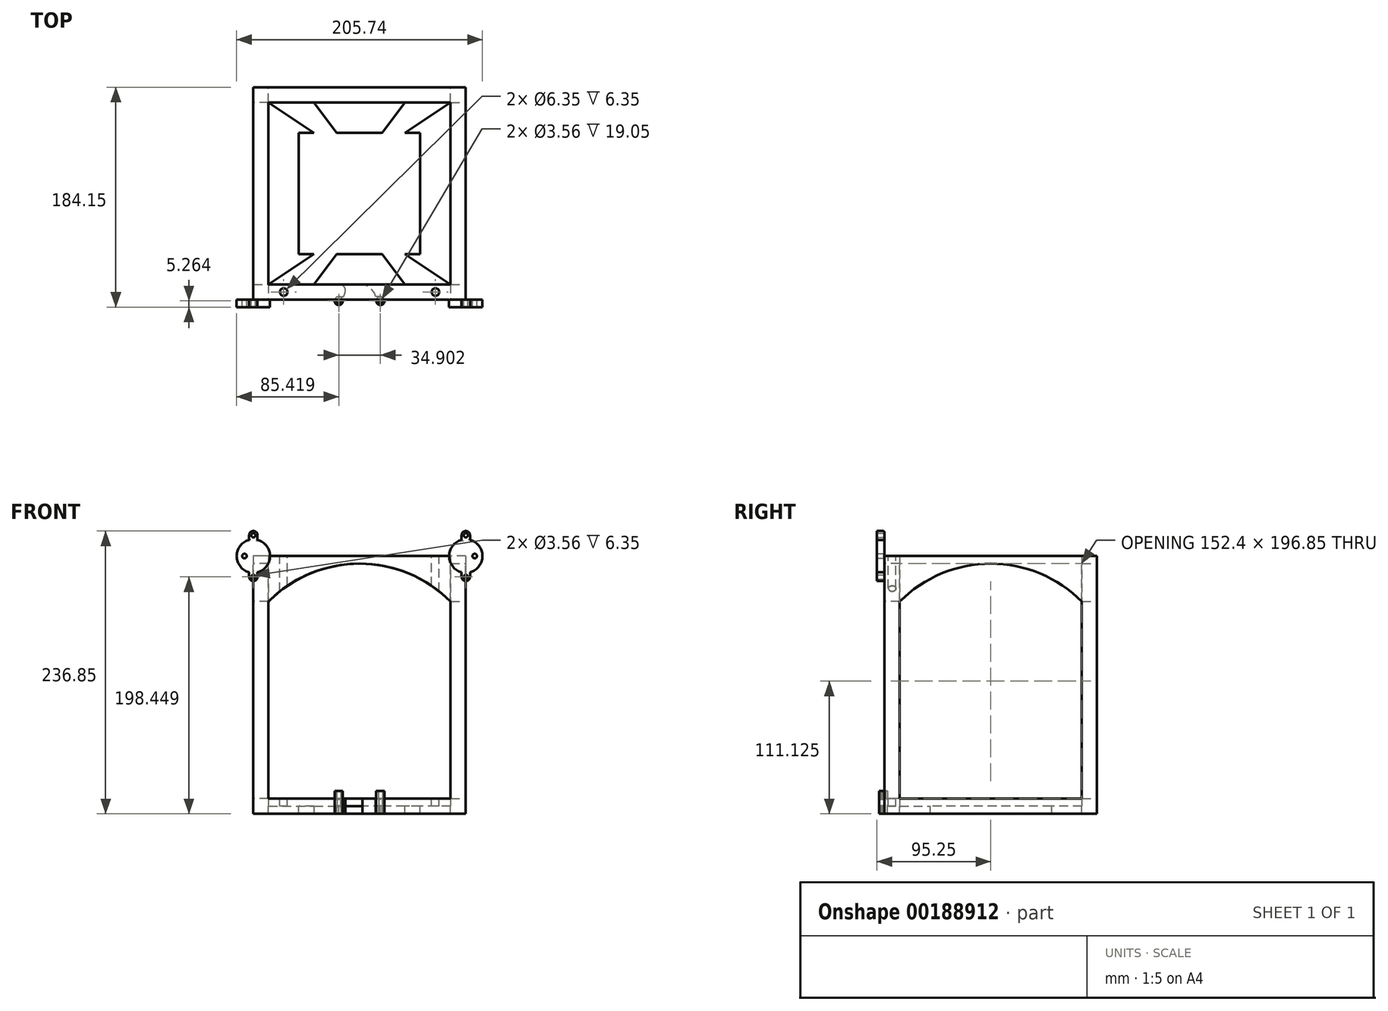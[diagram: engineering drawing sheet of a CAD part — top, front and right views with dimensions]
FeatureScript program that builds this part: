
annotation { "Feature Type Name" : "Feature", "Feature Type Description" : "" }
export const myFeature = defineFeature(function(context is Context, id is Id, definition is map)
    precondition{}
    {
        {
            var Q0;
            Q0=qCreatedBy(makeId("Top.planeOp"),FACE);
            var sketch = newSketch(context, id + "F0", { "sketchPlane" : qUnion([Q0])});
            skLineSegment(sketch, "E0.bottom", {"start": v(50.8, 50.8) * mm, "end": v(-50.8, 50.8) * mm});
            skLineSegment(sketch, "E0.top", {"start": v(50.8, -50.8) * mm, "end": v(-50.8, -50.8) * mm});
            skLineSegment(sketch, "E0.left", {"start": v(50.8, 50.8) * mm, "end": v(50.8, -50.8) * mm});
            skLineSegment(sketch, "E0.right", {"start": v(-50.8, 50.8) * mm, "end": v(-50.8, -50.8) * mm});
            skPoint(sketch, "E0.middle", {"position": v(0, 0) * mm});
            skSolve(sketch);
        }
        {
            var Q0;
            Q0=qSketchRegion(id+"F0",true);
            extrude(context, id + "F1", {"entities" : qUnion([Q0]), "oppositeDirection" : true, "depth" : 6.35 * mm});
        }
        {
            var Q0;
            Q0=qCreatedBy(makeId("Right.planeOp"),FACE);
            var sketch = newSketch(context, id + "F2", { "sketchPlane" : qUnion([Q0])});
            skLineSegment(sketch, "E1.bottom", {"start": v(-76.2, 6.35) * mm, "end": v(-88.9, 6.35) * mm});
            skLineSegment(sketch, "E1.top", {"start": v(-76.2, -6.35) * mm, "end": v(-88.9, -6.35) * mm});
            skLineSegment(sketch, "E1.left", {"start": v(-76.2, 6.35) * mm, "end": v(-76.2, -6.35) * mm});
            skLineSegment(sketch, "E1.right", {"start": v(-88.9, 6.35) * mm, "end": v(-88.9, -6.35) * mm});
            skPoint(sketch, "E1.middle", {"position": v(-82.55, 0) * mm});
            skSolve(sketch);
        }
        {
            var Q0;
            Q0=qSketchRegion(id+"F2",true);
            extrude(context, id + "F3", {"entities" : qUnion([Q0]), "endBound" : BoundingType.SYMMETRIC, "depth" : 177.8 * mm});
        }
        {
            var Q0;
            Q0=makeQuery(id+"F3.opExtrude","SWEPT_BODY",BODY,{"disambiguationData":[OSD([sQuery(id+"F2.wireOp",EDGE,"E1.bottom"),sQuery(id+"F2.wireOp",EDGE,"E1.top"),sQuery(id+"F2.wireOp",EDGE,"E1.left"),sQuery(id+"F2.wireOp",EDGE,"E1.right")])]});
            var Q1;
            Q1=qCreatedBy(makeId("Front.planeOp"),FACE);
            mirror(context, id + "F4", {"entities" : qUnion([Q0]), "mirrorPlane" : qUnion([Q1])});
        }
        {
            var Q0;
            Q0=qCreatedBy(makeId("Front.planeOp"),FACE);
            var sketch = newSketch(context, id + "F5", { "sketchPlane" : qUnion([Q0])});
            skLineSegment(sketch, "E2", {"start": v(76.2, 6.35) * mm, "end": v(76.2, -6.35) * mm});
            skLineSegment(sketch, "E3", {"start": v(76.2, -6.35) * mm, "end": v(88.9, -6.35) * mm});
            skLineSegment(sketch, "E4", {"start": v(88.9, -6.35) * mm, "end": v(88.9, 6.35) * mm});
            skLineSegment(sketch, "E5", {"start": v(88.9, 6.35) * mm, "end": v(76.2, 6.35) * mm});
            skSolve(sketch);
        }
        {
            var Q0;
            Q0=qSketchRegion(id+"F5",true);
            extrude(context, id + "F6", {"entities" : qUnion([Q0]), "endBound" : BoundingType.SYMMETRIC, "depth" : 152.4 * mm});
        }
        {
            var Q0;
            Q0=makeQuery(id+"F6.opExtrude","SWEPT_BODY",BODY,{"disambiguationData":[OSD([sQuery(id+"F5.wireOp",EDGE,"E2"),sQuery(id+"F5.wireOp",EDGE,"E3"),sQuery(id+"F5.wireOp",EDGE,"E4"),sQuery(id+"F5.wireOp",EDGE,"E5")])]});
            var Q1;
            Q1=qCreatedBy(makeId("Right.planeOp"),FACE);
            mirror(context, id + "F7", {"entities" : qUnion([Q0]), "mirrorPlane" : qUnion([Q1])});
        }
        {
            var Q0;
            Q0=makeQuery(id+"F1.opExtrude","SWEPT_FACE",FACE,{"disambiguationData":[OSD([sQuery(id+"F0.wireOp",EDGE,"E0.top")])]});
            var sketch = newSketch(context, id + "F8", { "sketchPlane" : qUnion([Q0])});
            skLineSegment(sketch, "E6", {"start": v(-38.1, 0) * mm, "end": v(-38.1, -6.35) * mm});
            skLineSegment(sketch, "E7", {"start": v(-38.1, -6.35) * mm, "end": v(-19.05, -6.35) * mm});
            skLineSegment(sketch, "E8", {"start": v(-19.05, -6.35) * mm, "end": v(-19.05, 0) * mm});
            skLineSegment(sketch, "E9", {"start": v(-19.05, 0) * mm, "end": v(-38.1, 0) * mm});
            skLineSegment(sketch, "E10.MirrorCS", {"start": v(19.05, -6.35) * mm, "end": v(19.05, 0) * mm, "construction": true});
            skLineSegment(sketch, "E11.MirrorCS", {"start": v(19.05, 0) * mm, "end": v(38.1, 0) * mm, "construction": true});
            skLineSegment(sketch, "E12.MirrorCS", {"start": v(38.1, 0) * mm, "end": v(38.1, -6.35) * mm, "construction": true});
            skLineSegment(sketch, "E13.MirrorCS", {"start": v(38.1, -6.35) * mm, "end": v(19.05, -6.35) * mm, "construction": true});
            skSolve(sketch);
        }
        {
            var Q0;
            Q0=makeQuery(id+"F3.opExtrude","SWEPT_FACE",FACE,{"disambiguationData":[OSD([sQuery(id+"F2.wireOp",EDGE,"E1.left")])]});
            var sketch = newSketch(context, id + "F9", { "sketchPlane" : qUnion([Q0])});
            skLineSegment(sketch, "E14.bottom", {"start": v(-76.2, -6.35) * mm, "end": v(-38.1, -6.35) * mm, "construction": true});
            skLineSegment(sketch, "E14.top", {"start": v(-76.2, 0) * mm, "end": v(-38.1, 0) * mm, "construction": true});
            skLineSegment(sketch, "E14.left", {"start": v(-76.2, -6.35) * mm, "end": v(-76.2, 0) * mm, "construction": true});
            skLineSegment(sketch, "E14.right", {"start": v(-38.1, -6.35) * mm, "end": v(-38.1, 0) * mm, "construction": true});
            skLineSegment(sketch, "E15.MirrorCS", {"start": v(76.2, 0) * mm, "end": v(38.1, 0) * mm});
            skLineSegment(sketch, "E16.MirrorCS", {"start": v(38.1, -6.35) * mm, "end": v(38.1, 0) * mm});
            skLineSegment(sketch, "E17.MirrorCS", {"start": v(76.2, -6.35) * mm, "end": v(38.1, -6.35) * mm});
            skLineSegment(sketch, "E18.MirrorCS", {"start": v(76.2, -6.35) * mm, "end": v(76.2, 0) * mm});
            skSolve(sketch);
        }
        {
            var Q0;
            Q0=makeQuery(id+"F9.imprint","IMPRINT",FACE,{"disambiguationData":[TD([[makeQuery(id+"F9.imprint","IMPRINT",EDGE,{"derivedFrom":sQuery(id+"F9.wireOp",EDGE,"E15.MirrorCS")}),1.0]])]});
            var Q1;
            Q1=makeQuery(id+"F8.imprint","IMPRINT",FACE,{"disambiguationData":[TD([[makeQuery(id+"F8.imprint","IMPRINT",EDGE,{"derivedFrom":sQuery(id+"F8.wireOp",EDGE,"E6")}),1.0]])]});
            loft(context, id + "F10", {"sheetProfilesArray" : [{ "sheetProfileEntities" : qUnion([Q0]) }, { "sheetProfileEntities" : qUnion([Q1]) }]});
        }
        {
            var Q0;
            Q0=makeQuery(id+"F10.opLoft","SWEPT_BODY",BODY,{"disambiguationData":[OSD([makeQuery(id+"F8.imprint","IMPRINT",FACE,{"disambiguationData":[TD([[makeQuery(id+"F8.imprint","IMPRINT",EDGE,{"derivedFrom":sQuery(id+"F8.wireOp",EDGE,"E6")}),1.0]])]}),makeQuery(id+"F9.imprint","IMPRINT",FACE,{"disambiguationData":[TD([[makeQuery(id+"F9.imprint","IMPRINT",EDGE,{"derivedFrom":sQuery(id+"F9.wireOp",EDGE,"E15.MirrorCS")}),1.0]])]})])]});
            var Q1;
            Q1=qCreatedBy(makeId("Right.planeOp"),FACE);
            mirror(context, id + "F11", {"entities" : qUnion([Q0]), "mirrorPlane" : qUnion([Q1])});
        }
        {
            var Q0;
            Q0=makeQuery(id+"F11.opPattern","COPY",BODY,{"derivedFrom":makeQuery(id+"F10.opLoft","SWEPT_BODY",BODY,{"disambiguationData":[OSD([makeQuery(id+"F8.imprint","IMPRINT",FACE,{"disambiguationData":[TD([[makeQuery(id+"F8.imprint","IMPRINT",EDGE,{"derivedFrom":sQuery(id+"F8.wireOp",EDGE,"E6")}),1.0]])]}),makeQuery(id+"F9.imprint","IMPRINT",FACE,{"disambiguationData":[TD([[makeQuery(id+"F9.imprint","IMPRINT",EDGE,{"derivedFrom":sQuery(id+"F9.wireOp",EDGE,"E15.MirrorCS")}),1.0]])]})])]}),"instanceName":"1"});
            var Q1;
            Q1=makeQuery(id+"F10.opLoft","SWEPT_BODY",BODY,{"disambiguationData":[OSD([makeQuery(id+"F8.imprint","IMPRINT",FACE,{"disambiguationData":[TD([[makeQuery(id+"F8.imprint","IMPRINT",EDGE,{"derivedFrom":sQuery(id+"F8.wireOp",EDGE,"E6")}),1.0]])]}),makeQuery(id+"F9.imprint","IMPRINT",FACE,{"disambiguationData":[TD([[makeQuery(id+"F9.imprint","IMPRINT",EDGE,{"derivedFrom":sQuery(id+"F9.wireOp",EDGE,"E15.MirrorCS")}),1.0]])]})])]});
            var Q2;
            Q2=qCreatedBy(makeId("Front.planeOp"),FACE);
            mirror(context, id + "F12", {"entities" : qUnion([Q0, Q1]), "mirrorPlane" : qUnion([Q2])});
        }
        {
            var Q0;
            Q0=makeQuery(id+"F1.opExtrude","SWEPT_BODY",BODY,{"disambiguationData":[OSD([sQuery(id+"F0.wireOp",EDGE,"E0.bottom"),sQuery(id+"F0.wireOp",EDGE,"E0.top"),sQuery(id+"F0.wireOp",EDGE,"E0.left"),sQuery(id+"F0.wireOp",EDGE,"E0.right")])]});
            var Q1;
            Q1=makeQuery(id+"F7.opPattern","COPY",BODY,{"derivedFrom":makeQuery(id+"F6.opExtrude","SWEPT_BODY",BODY,{"disambiguationData":[OSD([sQuery(id+"F5.wireOp",EDGE,"E2"),sQuery(id+"F5.wireOp",EDGE,"E3"),sQuery(id+"F5.wireOp",EDGE,"E4"),sQuery(id+"F5.wireOp",EDGE,"E5")])]}),"instanceName":"1"});
            var Q2;
            Q2=makeQuery(id+"F12.opPattern","COPY",BODY,{"derivedFrom":makeQuery(id+"F10.opLoft","SWEPT_BODY",BODY,{"disambiguationData":[OSD([makeQuery(id+"F8.imprint","IMPRINT",FACE,{"disambiguationData":[TD([[makeQuery(id+"F8.imprint","IMPRINT",EDGE,{"derivedFrom":sQuery(id+"F8.wireOp",EDGE,"E6")}),1.0]])]}),makeQuery(id+"F9.imprint","IMPRINT",FACE,{"disambiguationData":[TD([[makeQuery(id+"F9.imprint","IMPRINT",EDGE,{"derivedFrom":sQuery(id+"F9.wireOp",EDGE,"E15.MirrorCS")}),1.0]])]})])]}),"instanceName":"1"});
            var Q3;
            Q3=makeQuery(id+"F4.opPattern","COPY",BODY,{"derivedFrom":makeQuery(id+"F3.opExtrude","SWEPT_BODY",BODY,{"disambiguationData":[OSD([sQuery(id+"F2.wireOp",EDGE,"E1.bottom"),sQuery(id+"F2.wireOp",EDGE,"E1.top"),sQuery(id+"F2.wireOp",EDGE,"E1.left"),sQuery(id+"F2.wireOp",EDGE,"E1.right")])]}),"instanceName":"1"});
            var Q4;
            Q4=makeQuery(id+"F3.opExtrude","SWEPT_BODY",BODY,{"disambiguationData":[OSD([sQuery(id+"F2.wireOp",EDGE,"E1.bottom"),sQuery(id+"F2.wireOp",EDGE,"E1.top"),sQuery(id+"F2.wireOp",EDGE,"E1.left"),sQuery(id+"F2.wireOp",EDGE,"E1.right")])]});
            var Q5;
            Q5=makeQuery(id+"F6.opExtrude","SWEPT_BODY",BODY,{"disambiguationData":[OSD([sQuery(id+"F5.wireOp",EDGE,"E2"),sQuery(id+"F5.wireOp",EDGE,"E3"),sQuery(id+"F5.wireOp",EDGE,"E4"),sQuery(id+"F5.wireOp",EDGE,"E5")])]});
            var Q6;
            Q6=makeQuery(id+"F11.opPattern","COPY",BODY,{"derivedFrom":makeQuery(id+"F10.opLoft","SWEPT_BODY",BODY,{"disambiguationData":[OSD([makeQuery(id+"F8.imprint","IMPRINT",FACE,{"disambiguationData":[TD([[makeQuery(id+"F8.imprint","IMPRINT",EDGE,{"derivedFrom":sQuery(id+"F8.wireOp",EDGE,"E6")}),1.0]])]}),makeQuery(id+"F9.imprint","IMPRINT",FACE,{"disambiguationData":[TD([[makeQuery(id+"F9.imprint","IMPRINT",EDGE,{"derivedFrom":sQuery(id+"F9.wireOp",EDGE,"E15.MirrorCS")}),1.0]])]})])]}),"instanceName":"1"});
            var Q7;
            Q7=makeQuery(id+"F10.opLoft","SWEPT_BODY",BODY,{"disambiguationData":[OSD([makeQuery(id+"F8.imprint","IMPRINT",FACE,{"disambiguationData":[TD([[makeQuery(id+"F8.imprint","IMPRINT",EDGE,{"derivedFrom":sQuery(id+"F8.wireOp",EDGE,"E6")}),1.0]])]}),makeQuery(id+"F9.imprint","IMPRINT",FACE,{"disambiguationData":[TD([[makeQuery(id+"F9.imprint","IMPRINT",EDGE,{"derivedFrom":sQuery(id+"F9.wireOp",EDGE,"E15.MirrorCS")}),1.0]])]})])]});
            var Q8;
            Q8=makeQuery(id+"F12.opPattern","COPY",BODY,{"derivedFrom":makeQuery(id+"F11.opPattern","COPY",BODY,{"derivedFrom":makeQuery(id+"F10.opLoft","SWEPT_BODY",BODY,{"disambiguationData":[OSD([makeQuery(id+"F8.imprint","IMPRINT",FACE,{"disambiguationData":[TD([[makeQuery(id+"F8.imprint","IMPRINT",EDGE,{"derivedFrom":sQuery(id+"F8.wireOp",EDGE,"E6")}),1.0]])]}),makeQuery(id+"F9.imprint","IMPRINT",FACE,{"disambiguationData":[TD([[makeQuery(id+"F9.imprint","IMPRINT",EDGE,{"derivedFrom":sQuery(id+"F9.wireOp",EDGE,"E15.MirrorCS")}),1.0]])]})])]}),"instanceName":"1"}),"instanceName":"1"});
            booleanBodies(context, id + "F13", {"operationType" : BooleanOperationType.UNION, "tools" : qUnion([Q0, Q1, Q2, Q3, Q4, Q5, Q6, Q7, Q8])});
        }
        {
            var Q0;
            {var subQ0=makeQuery(id+"F6.opExtrude","SWEPT_FACE",FACE,{"disambiguationData":[OSD([sQuery(id+"F5.wireOp",EDGE,"E5")])]});var subQ1=makeQuery(id+"F3.opExtrude","SWEPT_FACE",FACE,{"disambiguationData":[OSD([sQuery(id+"F2.wireOp",EDGE,"E1.bottom")])]});Q0=makeQuery(id+"F13.opBoolean","MERGE",FACE,{"derivedFrom":[subQ1,makeQuery(id+"F4.opPattern","COPY",FACE,{"derivedFrom":subQ1,"instanceName":"1"}),subQ0,makeQuery(id+"F7.opPattern","COPY",FACE,{"derivedFrom":subQ0,"instanceName":"1"})]});}
            var sketch = newSketch(context, id + "F14", { "sketchPlane" : qUnion([Q0])});
            skLineSegment(sketch, "E19.bottom", {"start": v(-76.2, 76.2) * mm, "end": v(-88.9, 76.2) * mm});
            skLineSegment(sketch, "E19.top", {"start": v(-76.2, 88.9) * mm, "end": v(-88.9, 88.9) * mm});
            skLineSegment(sketch, "E19.left", {"start": v(-76.2, 76.2) * mm, "end": v(-76.2, 88.9) * mm});
            skLineSegment(sketch, "E19.right", {"start": v(-88.9, 76.2) * mm, "end": v(-88.9, 88.9) * mm});
            skLineSegment(sketch, "E20.bottom", {"start": v(76.2, 76.2) * mm, "end": v(88.9, 76.2) * mm});
            skLineSegment(sketch, "E20.top", {"start": v(76.2, 88.9) * mm, "end": v(88.9, 88.9) * mm});
            skLineSegment(sketch, "E20.left", {"start": v(76.2, 76.2) * mm, "end": v(76.2, 88.9) * mm});
            skLineSegment(sketch, "E20.right", {"start": v(88.9, 76.2) * mm, "end": v(88.9, 88.9) * mm});
            skLineSegment(sketch, "E21.bottom", {"start": v(76.2, -76.2) * mm, "end": v(88.9, -76.2) * mm});
            skLineSegment(sketch, "E21.top", {"start": v(76.2, -88.9) * mm, "end": v(88.9, -88.9) * mm});
            skLineSegment(sketch, "E21.left", {"start": v(76.2, -76.2) * mm, "end": v(76.2, -88.9) * mm});
            skLineSegment(sketch, "E21.right", {"start": v(88.9, -76.2) * mm, "end": v(88.9, -88.9) * mm});
            skLineSegment(sketch, "E22.bottom", {"start": v(-88.9, -88.9) * mm, "end": v(-76.2, -88.9) * mm});
            skLineSegment(sketch, "E22.top", {"start": v(-88.9, -76.2) * mm, "end": v(-76.2, -76.2) * mm});
            skLineSegment(sketch, "E22.left", {"start": v(-88.9, -88.9) * mm, "end": v(-88.9, -76.2) * mm});
            skLineSegment(sketch, "E22.right", {"start": v(-76.2, -88.9) * mm, "end": v(-76.2, -76.2) * mm});
            skSolve(sketch);
        }
        {
            var Q0;
            Q0=qSketchRegion(id+"F14",true);
            extrude(context, id + "F15", {"entities" : qUnion([Q0]), "operationType" : NewBodyOperationType.ADD, "depth" : 203.2 * mm});
        }
        {
            var Q0;
            {var subQ0=makeQuery(id+"F3.opExtrude","CAP_FACE",FACE,{"disambiguationData":[OSD([sQuery(id+"F2.wireOp",EDGE,"E1.bottom"),sQuery(id+"F2.wireOp",EDGE,"E1.top"),sQuery(id+"F2.wireOp",EDGE,"E1.left"),sQuery(id+"F2.wireOp",EDGE,"E1.right")])],"isStart":true});Q0=makeQuery(id+"F15.boolean.opBoolean","MERGE",FACE,{"derivedFrom":[makeQuery(id+"F13.opBoolean","MERGE",FACE,{"derivedFrom":[subQ0,makeQuery(id+"F4.opPattern","COPY",FACE,{"derivedFrom":subQ0,"instanceName":"1"}),makeQuery(id+"F7.opPattern","COPY",FACE,{"derivedFrom":makeQuery(id+"F6.opExtrude","SWEPT_FACE",FACE,{"disambiguationData":[OSD([sQuery(id+"F5.wireOp",EDGE,"E4")])]}),"instanceName":"1"})]}),makeQuery(id+"F15.opExtrude","SWEPT_FACE",FACE,{"disambiguationData":[OSD([sQuery(id+"F14.wireOp",EDGE,"E19.right")])]}),makeQuery(id+"F15.opExtrude","SWEPT_FACE",FACE,{"disambiguationData":[OSD([sQuery(id+"F14.wireOp",EDGE,"E22.left")])]})]});}
            var sketch = newSketch(context, id + "F16", { "sketchPlane" : qUnion([Q0])});
            skArc(sketch, "E23", {"start": v(76.2, 171.45) * mm, "mid": v(0, 203.2) * mm, "end": v(-76.2, 171.45) * mm});
            skLineSegment(sketch, "E24", {"start": v(-76.2, 209.55) * mm, "end": v(76.2, 209.55) * mm});
            skLineSegment(sketch, "E25", {"start": v(76.2, 209.55) * mm, "end": v(76.2, 171.45) * mm});
            skLineSegment(sketch, "E26", {"start": v(-76.2, 209.55) * mm, "end": v(-76.2, 171.45) * mm});
            skSolve(sketch);
        }
        {
            var Q0;
            Q0=qSketchRegion(id+"F16",true);
            extrude(context, id + "F17", {"entities" : qUnion([Q0]), "oppositeDirection" : true, "depth" : 12.7 * mm});
        }
        {
            var Q0;
            Q0=makeQuery(id+"F17.opExtrude","SWEPT_BODY",BODY,{"disambiguationData":[OSD([sQuery(id+"F16.wireOp",EDGE,"E23"),sQuery(id+"F16.wireOp",EDGE,"E24"),sQuery(id+"F16.wireOp",EDGE,"E25"),sQuery(id+"F16.wireOp",EDGE,"E26")])]});
            var Q1;
            Q1=qCreatedBy(makeId("Right.planeOp"),FACE);
            mirror(context, id + "F18", {"operationType" : NewBodyOperationType.ADD, "entities" : qUnion([Q0]), "mirrorPlane" : qUnion([Q1])});
        }
        {
            var Q0;
            Q0=makeQuery(id+"F15.boolean.opBoolean","MERGE",FACE,{"derivedFrom":[makeQuery(id+"F4.opPattern","COPY",FACE,{"derivedFrom":makeQuery(id+"F3.opExtrude","SWEPT_FACE",FACE,{"disambiguationData":[OSD([sQuery(id+"F2.wireOp",EDGE,"E1.right")])]}),"instanceName":"1"}),makeQuery(id+"F15.opExtrude","SWEPT_FACE",FACE,{"disambiguationData":[OSD([sQuery(id+"F14.wireOp",EDGE,"E19.top")])]}),makeQuery(id+"F15.opExtrude","SWEPT_FACE",FACE,{"disambiguationData":[OSD([sQuery(id+"F14.wireOp",EDGE,"E20.top")])]})]});
            var sketch = newSketch(context, id + "F19", { "sketchPlane" : qUnion([Q0])});
            skArc(sketch, "E27", {"start": v(76.2, 171.45) * mm, "mid": v(0, 203.2) * mm, "end": v(-76.2, 171.45) * mm});
            skLineSegment(sketch, "E28", {"start": v(-76.2, 171.45) * mm, "end": v(-76.2, 209.55) * mm});
            skLineSegment(sketch, "E29", {"start": v(-76.2, 209.55) * mm, "end": v(76.2, 209.55) * mm});
            skLineSegment(sketch, "E30", {"start": v(76.2, 209.55) * mm, "end": v(76.2, 171.45) * mm});
            skSolve(sketch);
        }
        {
            var Q0;
            Q0=qSketchRegion(id+"F19",true);
            extrude(context, id + "F20", {"entities" : qUnion([Q0]), "oppositeDirection" : true, "depth" : 12.7 * mm});
        }
        {
            var Q0;
            Q0=makeQuery(id+"F20.opExtrude","SWEPT_BODY",BODY,{"disambiguationData":[OSD([sQuery(id+"F19.wireOp",EDGE,"E27"),sQuery(id+"F19.wireOp",EDGE,"E28"),sQuery(id+"F19.wireOp",EDGE,"E29"),sQuery(id+"F19.wireOp",EDGE,"E30")])]});
            var Q1;
            Q1=qCreatedBy(makeId("Front.planeOp"),FACE);
            mirror(context, id + "F21", {"operationType" : NewBodyOperationType.ADD, "entities" : qUnion([Q0]), "mirrorPlane" : qUnion([Q1])});
        }
        {
            var Q0;
            {var subQ0=makeQuery(id+"F20.opExtrude","SWEPT_FACE",FACE,{"disambiguationData":[OSD([sQuery(id+"F19.wireOp",EDGE,"E29")])]});var subQ1=makeQuery(id+"F17.opExtrude","SWEPT_FACE",FACE,{"disambiguationData":[OSD([sQuery(id+"F16.wireOp",EDGE,"E24")])]});Q0=makeQuery(id+"F21.boolean.opBoolean","MERGE",FACE,{"derivedFrom":[makeQuery(id+"F18.boolean.opBoolean","MERGE",FACE,{"derivedFrom":[makeQuery(id+"F15.opExtrude","CAP_FACE",FACE,{"disambiguationData":[OSD([sQuery(id+"F14.wireOp",EDGE,"E19.bottom"),sQuery(id+"F14.wireOp",EDGE,"E19.top"),sQuery(id+"F14.wireOp",EDGE,"E19.left"),sQuery(id+"F14.wireOp",EDGE,"E19.right")])],"isStart":false}),makeQuery(id+"F15.opExtrude","CAP_FACE",FACE,{"disambiguationData":[OSD([sQuery(id+"F14.wireOp",EDGE,"E22.bottom"),sQuery(id+"F14.wireOp",EDGE,"E22.top"),sQuery(id+"F14.wireOp",EDGE,"E22.left"),sQuery(id+"F14.wireOp",EDGE,"E22.right")])],"isStart":false}),subQ1]}),makeQuery(id+"F18.boolean.opBoolean","MERGE",FACE,{"derivedFrom":[makeQuery(id+"F15.opExtrude","CAP_FACE",FACE,{"disambiguationData":[OSD([sQuery(id+"F14.wireOp",EDGE,"E20.bottom"),sQuery(id+"F14.wireOp",EDGE,"E20.top"),sQuery(id+"F14.wireOp",EDGE,"E20.left"),sQuery(id+"F14.wireOp",EDGE,"E20.right")])],"isStart":false}),makeQuery(id+"F15.opExtrude","CAP_FACE",FACE,{"disambiguationData":[OSD([sQuery(id+"F14.wireOp",EDGE,"E21.bottom"),sQuery(id+"F14.wireOp",EDGE,"E21.top"),sQuery(id+"F14.wireOp",EDGE,"E21.left"),sQuery(id+"F14.wireOp",EDGE,"E21.right")])],"isStart":false}),makeQuery(id+"F18.opPattern","COPY",FACE,{"derivedFrom":subQ1,"instanceName":"1"})]}),subQ0,makeQuery(id+"F21.opPattern","COPY",FACE,{"derivedFrom":subQ0,"instanceName":"1"})]});}
            var sketch = newSketch(context, id + "F22", { "sketchPlane" : qUnion([Q0])});
            skCircle(sketch, "E31", {"center": v(-63.5, -82.55) * mm, "radius": 3.18 * mm});
            skCircle(sketch, "E32", {"center": v(63.5, -82.55) * mm, "radius": 3.18 * mm});
            skLineSegment(sketch, "E33", {"start": v(-63.5, -82.55) * mm, "end": v(63.5, -82.55) * mm, "construction": true});
            skLineSegment(sketch, "E34", {"start": v(63.5, -82.55) * mm, "end": v(0, 0) * mm, "construction": true});
            skLineSegment(sketch, "E35", {"start": v(0, 0) * mm, "end": v(-63.5, -82.55) * mm, "construction": true});
            skLineSegment(sketch, "E36", {"start": v(0, -76.2) * mm, "end": v(0, -82.55) * mm, "construction": true});
            skLineSegment(sketch, "E37", {"start": v(0, -82.55) * mm, "end": v(0, -88.9) * mm, "construction": true});
            skSolve(sketch);
        }
        {
            var Q0;
            Q0=qSketchRegion(id+"F22",true);
            extrude(context, id + "F23", {"entities" : qUnion([Q0]), "operationType" : NewBodyOperationType.REMOVE, "oppositeDirection" : true, "depth" : 209.55 * mm});
        }
        {
            var Q0;
            {var subQ0=sQuery(id+"F2.wireOp",EDGE,"E1.top");var subQ1=sQuery(id+"F0.wireOp",EDGE,"E0.top");var subQ2=makeQuery(id+"F10.opLoft","SWEPT_FACE",FACE,{"disambiguationData":[OSD([subQ1,subQ0,sQuery(id+"F2.wireOp",EDGE,"E1.left"),sQuery(id+"F8.wireOp",EDGE,"E6"),sQuery(id+"F8.wireOp",EDGE,"E7"),sQuery(id+"F8.wireOp",EDGE,"E8"),sQuery(id+"F9.wireOp",EDGE,"E16.MirrorCS"),sQuery(id+"F9.wireOp",EDGE,"E17.MirrorCS"),sQuery(id+"F9.wireOp",EDGE,"E18.MirrorCS")])]});var subQ3=makeQuery(id+"F11.opPattern","COPY",FACE,{"derivedFrom":subQ2,"instanceName":"1"});var subQ4=makeQuery(id+"F6.opExtrude","SWEPT_FACE",FACE,{"disambiguationData":[OSD([sQuery(id+"F5.wireOp",EDGE,"E3")])]});var subQ5=makeQuery(id+"F3.opExtrude","SWEPT_FACE",FACE,{"disambiguationData":[OSD([subQ0])]});Q0=makeQuery(id+"F13.opBoolean","MERGE",FACE,{"derivedFrom":[makeQuery(id+"F1.opExtrude","CAP_FACE",FACE,{"disambiguationData":[OSD([sQuery(id+"F0.wireOp",EDGE,"E0.bottom"),subQ1,sQuery(id+"F0.wireOp",EDGE,"E0.left"),sQuery(id+"F0.wireOp",EDGE,"E0.right")])],"isStart":false}),subQ5,makeQuery(id+"F4.opPattern","COPY",FACE,{"derivedFrom":subQ5,"instanceName":"1"}),subQ4,makeQuery(id+"F7.opPattern","COPY",FACE,{"derivedFrom":subQ4,"instanceName":"1"}),subQ2,subQ3,makeQuery(id+"F12.opPattern","COPY",FACE,{"derivedFrom":subQ2,"instanceName":"1"}),makeQuery(id+"F12.opPattern","COPY",FACE,{"derivedFrom":subQ3,"instanceName":"1"})]});}
            var sketch = newSketch(context, id + "F24", { "sketchPlane" : qUnion([Q0])});
            skCircle(sketch, "E38", {"center": v(0, 82.55) * mm, "radius": 1.9 * mm});
            skArc(sketch, "E39", {"start": v(13.52, 93.49) * mm, "mid": v(0, 103.96) * mm, "end": v(-13.52, 93.49) * mm});
            skArc(sketch, "E40", {"start": v(17.45, 86.49) * mm, "mid": v(20.95, 89.99) * mm, "end": v(17.45, 93.49) * mm});
            skArc(sketch, "E41", {"start": v(-17.45, 93.49) * mm, "mid": v(-20.95, 89.99) * mm, "end": v(-17.45, 86.49) * mm});
            skLineSegment(sketch, "E42", {"start": v(17.45, 89.99) * mm, "end": v(0, 89.99) * mm, "construction": true});
            skLineSegment(sketch, "E43", {"start": v(0, 89.99) * mm, "end": v(-17.45, 89.99) * mm, "construction": true});
            skLineSegment(sketch, "E44", {"start": v(0, 82.55) * mm, "end": v(0, 76.02) * mm, "construction": true});
            skLineSegment(sketch, "E45", {"start": v(17.45, 89.99) * mm, "end": v(0, 82.55) * mm, "construction": true});
            skLineSegment(sketch, "E46", {"start": v(0, 82.55) * mm, "end": v(-17.45, 89.99) * mm, "construction": true});
            skLineSegment(sketch, "E47", {"start": v(17.45, 93.49) * mm, "end": v(13.52, 93.49) * mm});
            skLineSegment(sketch, "E48", {"start": v(17.45, 86.49) * mm, "end": v(13.52, 86.49) * mm});
            skLineSegment(sketch, "E49", {"start": v(17.45, 93.49) * mm, "end": v(17.45, 89.99) * mm, "construction": true});
            skLineSegment(sketch, "E50", {"start": v(17.45, 86.49) * mm, "end": v(17.45, 89.99) * mm, "construction": true});
            skLineSegment(sketch, "E51", {"start": v(-17.45, 93.49) * mm, "end": v(-13.52, 93.49) * mm});
            skLineSegment(sketch, "E52", {"start": v(-17.45, 86.49) * mm, "end": v(-13.52, 86.49) * mm});
            skLineSegment(sketch, "E53", {"start": v(-17.45, 93.49) * mm, "end": v(-17.45, 89.99) * mm, "construction": true});
            skLineSegment(sketch, "E54", {"start": v(-17.45, 89.99) * mm, "end": v(-17.45, 86.49) * mm, "construction": true});
            skArc(sketch, "E55.trimOffspring", {"start": v(-13.52, 86.49) * mm, "mid": v(0, 76.02) * mm, "end": v(13.52, 86.49) * mm});
            skCircle(sketch, "E56", {"center": v(17.45, 89.99) * mm, "radius": 1.78 * mm});
            skCircle(sketch, "E57.MirrorC", {"center": v(-17.45, 89.99) * mm, "radius": 1.78 * mm});
            skPoint(sketch, "E58", {"position": v(0, 88.9) * mm});
            skLineSegment(sketch, "E59", {"start": v(0, 88.9) * mm, "end": v(0, 82.55) * mm, "construction": true});
            skLineSegment(sketch, "E60", {"start": v(0, 82.55) * mm, "end": v(0, 76.2) * mm, "construction": true});
            skSolve(sketch);
        }
        {
            var Q0;
            Q0=qSketchRegion(id+"F24",true);
            extrude(context, id + "F25", {"entities" : qUnion([Q0]), "operationType" : NewBodyOperationType.ADD, "oppositeDirection" : true, "depth" : 19.05 * mm});
        }
        {
            var Q0;
            Q0=makeQuery(id+"F25.opExtrude","CAP_FACE",FACE,{"disambiguationData":[OSD([sQuery(id+"F24.wireOp",EDGE,"E38"),sQuery(id+"F24.wireOp",EDGE,"E39"),sQuery(id+"F24.wireOp",EDGE,"E40"),sQuery(id+"F24.wireOp",EDGE,"E41"),sQuery(id+"F24.wireOp",EDGE,"E47"),sQuery(id+"F24.wireOp",EDGE,"E48"),sQuery(id+"F24.wireOp",EDGE,"E51"),sQuery(id+"F24.wireOp",EDGE,"E52"),sQuery(id+"F24.wireOp",EDGE,"E55.trimOffspring"),sQuery(id+"F24.wireOp",EDGE,"E56"),sQuery(id+"F24.wireOp",EDGE,"E57.MirrorC")])],"isStart":false});
            var sketch = newSketch(context, id + "F26", { "sketchPlane" : qUnion([Q0])});
            skArc(sketch, "E61", {"start": v(-13.97, -89.66) * mm, "mid": v(-13.97, -89.99) * mm, "end": v(-13.97, -90.31) * mm});
            skArc(sketch, "E62", {"start": v(-17.45, -93.49) * mm, "mid": v(-15.1, -92.57) * mm, "end": v(-13.97, -90.31) * mm});
            skArc(sketch, "E63", {"start": v(17.45, -86.49) * mm, "mid": v(13.95, -89.99) * mm, "end": v(17.45, -93.49) * mm});
            skLineSegment(sketch, "E64", {"start": v(-17.45, -86.49) * mm, "end": v(-13.52, -86.49) * mm});
            skLineSegment(sketch, "E65", {"start": v(-17.45, -93.49) * mm, "end": v(-13.52, -93.49) * mm});
            skLineSegment(sketch, "E66", {"start": v(17.45, -93.49) * mm, "end": v(13.52, -93.49) * mm});
            skLineSegment(sketch, "E67", {"start": v(13.52, -86.49) * mm, "end": v(17.45, -86.49) * mm});
            skArc(sketch, "E68.trimOffspring", {"start": v(-13.52, -93.49) * mm, "mid": v(0, -103.96) * mm, "end": v(13.52, -93.49) * mm});
            skArc(sketch, "E69.trimOffspring", {"start": v(13.52, -86.49) * mm, "mid": v(0, -76.02) * mm, "end": v(-13.52, -86.49) * mm});
            skArc(sketch, "E70.trimOffspring", {"start": v(-13.97, -89.66) * mm, "mid": v(-15.1, -87.4) * mm, "end": v(-17.45, -86.49) * mm});
            skSolve(sketch);
        }
        {
            var Q0;
            Q0=qSketchRegion(id+"F26",true);
            extrude(context, id + "F27", {"entities" : qUnion([Q0]), "operationType" : NewBodyOperationType.REMOVE, "oppositeDirection" : true, "depth" : 25.4 * mm});
        }
        {
            var Q0;
            Q0=makeQuery(id+"F25.boolean.opBoolean","INTERSECT",EDGE,{"disambiguationData":[OD(1.0)],"derivedFrom":[makeQuery(id+"F3.opExtrude","SWEPT_FACE",FACE,{"disambiguationData":[OSD([sQuery(id+"F2.wireOp",EDGE,"E1.left")])]}),makeQuery(id+"F25.opExtrude","SWEPT_FACE",FACE,{"disambiguationData":[OSD([sQuery(id+"F24.wireOp",EDGE,"E55.trimOffspring")])]})]});
            var Q1;
            Q1=makeQuery(id+"F25.boolean.opBoolean","INTERSECT",EDGE,{"disambiguationData":[OD(0.0)],"derivedFrom":[makeQuery(id+"F3.opExtrude","SWEPT_FACE",FACE,{"disambiguationData":[OSD([sQuery(id+"F2.wireOp",EDGE,"E1.left")])]}),makeQuery(id+"F25.opExtrude","SWEPT_FACE",FACE,{"disambiguationData":[OSD([sQuery(id+"F24.wireOp",EDGE,"E55.trimOffspring")])]})]});
            fillet(context, id + "F28", {"entities" : qUnion([Q0, Q1]), "radius" : 5.08 * mm, "tangentPropagation" : true, "allowEdgeOverflow" : false});
        }
        {
            var Q0;
            {var subQ1=makeQuery(id+"F6.opExtrude","SWEPT_FACE",FACE,{"disambiguationData":[OSD([sQuery(id+"F5.wireOp",EDGE,"E4")])]});var subQ12=sQuery(id+"F2.wireOp",EDGE,"E1.right");var subQ16=sQuery(id+"F14.wireOp",EDGE,"E22.bottom");var subQ19=sQuery(id+"F19.wireOp",EDGE,"E29");var subQ30=sQuery(id+"F19.wireOp",EDGE,"E27");var subQ33=sQuery(id+"F14.wireOp",EDGE,"E21.top");Q0=makeQuery(id+"F25.boolean.opBoolean","SPLIT",FACE,{"disambiguationData":[TD([subQ1])],"derivedFrom":makeQuery(id+"F21.boolean.opBoolean","MERGE",FACE,{"derivedFrom":[makeQuery(id+"F15.boolean.opBoolean","MERGE",FACE,{"derivedFrom":[makeQuery(id+"F3.opExtrude","SWEPT_FACE",FACE,{"disambiguationData":[OSD([subQ12])]}),makeQuery(id+"F15.opExtrude","SWEPT_FACE",FACE,{"disambiguationData":[OSD([subQ33])]}),makeQuery(id+"F15.opExtrude","SWEPT_FACE",FACE,{"disambiguationData":[OSD([subQ16])]})]}),makeQuery(id+"F21.opPattern","COPY",FACE,{"derivedFrom":makeQuery(id+"F20.opExtrude","CAP_FACE",FACE,{"disambiguationData":[OSD([subQ30,sQuery(id+"F19.wireOp",EDGE,"E28"),subQ19,sQuery(id+"F19.wireOp",EDGE,"E30")])],"isStart":true}),"instanceName":"1"})]})});}
            var sketch = newSketch(context, id + "F29", { "sketchPlane" : qUnion([Q0])});
            skCircle(sketch, "E71", {"center": v(-96.34, 209.55) * mm, "radius": 1.9 * mm});
            skArc(sketch, "E72", {"start": v(-85.4, 196.03) * mm, "mid": v(-74.93, 209.55) * mm, "end": v(-85.4, 223.07) * mm});
            skArc(sketch, "E73", {"start": v(-92.4, 192.1) * mm, "mid": v(-88.9, 188.6) * mm, "end": v(-85.4, 192.1) * mm});
            skArc(sketch, "E74", {"start": v(-85.4, 227) * mm, "mid": v(-88.9, 230.5) * mm, "end": v(-92.4, 227) * mm});
            skLineSegment(sketch, "E75", {"start": v(-88.9, 192.1) * mm, "end": v(-88.9, 209.55) * mm, "construction": true});
            skLineSegment(sketch, "E76", {"start": v(-88.9, 209.55) * mm, "end": v(-88.9, 227) * mm, "construction": true});
            skLineSegment(sketch, "E77", {"start": v(-96.34, 209.55) * mm, "end": v(-102.87, 209.55) * mm, "construction": true});
            skLineSegment(sketch, "E78", {"start": v(-88.9, 192.1) * mm, "end": v(-96.34, 209.55) * mm, "construction": true});
            skLineSegment(sketch, "E79", {"start": v(-96.34, 209.55) * mm, "end": v(-88.9, 227) * mm, "construction": true});
            skLineSegment(sketch, "E80", {"start": v(-85.4, 192.1) * mm, "end": v(-85.4, 196.03) * mm});
            skLineSegment(sketch, "E81", {"start": v(-92.4, 192.1) * mm, "end": v(-92.4, 196.03) * mm});
            skLineSegment(sketch, "E82", {"start": v(-85.4, 192.1) * mm, "end": v(-88.9, 192.1) * mm, "construction": true});
            skLineSegment(sketch, "E83", {"start": v(-92.4, 192.1) * mm, "end": v(-88.9, 192.1) * mm, "construction": true});
            skLineSegment(sketch, "E84", {"start": v(-85.4, 227) * mm, "end": v(-85.4, 223.07) * mm});
            skLineSegment(sketch, "E85", {"start": v(-92.4, 227) * mm, "end": v(-92.4, 223.07) * mm});
            skLineSegment(sketch, "E86", {"start": v(-85.4, 227) * mm, "end": v(-88.9, 227) * mm, "construction": true});
            skLineSegment(sketch, "E87", {"start": v(-88.9, 227) * mm, "end": v(-92.4, 227) * mm, "construction": true});
            skArc(sketch, "E88.trimOffspring", {"start": v(-92.4, 223.07) * mm, "mid": v(-102.87, 209.55) * mm, "end": v(-92.4, 196.03) * mm});
            skCircle(sketch, "E89", {"center": v(-88.9, 192.1) * mm, "radius": 1.78 * mm});
            skCircle(sketch, "E90.MirrorC", {"center": v(-88.9, 227) * mm, "radius": 1.78 * mm});
            skCircle(sketch, "E91", {"center": v(96.34, 209.55) * mm, "radius": 1.9 * mm});
            skArc(sketch, "E92", {"start": v(85.4, 223.07) * mm, "mid": v(74.93, 209.55) * mm, "end": v(85.4, 196.03) * mm});
            skArc(sketch, "E93", {"start": v(92.4, 227) * mm, "mid": v(88.9, 230.5) * mm, "end": v(85.4, 227) * mm});
            skArc(sketch, "E94", {"start": v(85.4, 192.1) * mm, "mid": v(88.9, 188.6) * mm, "end": v(92.4, 192.1) * mm});
            skLineSegment(sketch, "E95", {"start": v(88.9, 227) * mm, "end": v(88.9, 209.55) * mm, "construction": true});
            skLineSegment(sketch, "E96", {"start": v(88.9, 209.55) * mm, "end": v(88.9, 192.1) * mm, "construction": true});
            skLineSegment(sketch, "E97", {"start": v(96.34, 209.55) * mm, "end": v(102.87, 209.55) * mm, "construction": true});
            skLineSegment(sketch, "E98", {"start": v(88.9, 227) * mm, "end": v(96.34, 209.55) * mm, "construction": true});
            skLineSegment(sketch, "E99", {"start": v(96.34, 209.55) * mm, "end": v(88.9, 192.1) * mm, "construction": true});
            skLineSegment(sketch, "E100", {"start": v(85.4, 227) * mm, "end": v(85.4, 223.07) * mm});
            skLineSegment(sketch, "E101", {"start": v(92.4, 227) * mm, "end": v(92.4, 223.07) * mm});
            skLineSegment(sketch, "E102", {"start": v(85.4, 227) * mm, "end": v(88.9, 227) * mm, "construction": true});
            skLineSegment(sketch, "E103", {"start": v(92.4, 227) * mm, "end": v(88.9, 227) * mm, "construction": true});
            skLineSegment(sketch, "E104", {"start": v(85.4, 192.1) * mm, "end": v(85.4, 196.03) * mm});
            skLineSegment(sketch, "E105", {"start": v(92.4, 192.1) * mm, "end": v(92.4, 196.03) * mm});
            skLineSegment(sketch, "E106", {"start": v(85.4, 192.1) * mm, "end": v(88.9, 192.1) * mm, "construction": true});
            skLineSegment(sketch, "E107", {"start": v(88.9, 192.1) * mm, "end": v(92.4, 192.1) * mm, "construction": true});
            skArc(sketch, "E108.trimOffspring", {"start": v(92.4, 196.03) * mm, "mid": v(102.87, 209.55) * mm, "end": v(92.4, 223.07) * mm});
            skCircle(sketch, "E109", {"center": v(88.9, 227) * mm, "radius": 1.78 * mm});
            skCircle(sketch, "E110.MirrorC", {"center": v(88.9, 192.1) * mm, "radius": 1.78 * mm});
            skSolve(sketch);
        }
        {
            var Q0;
            Q0=qSketchRegion(id+"F29",true);
            extrude(context, id + "F30", {"entities" : qUnion([Q0]), "operationType" : NewBodyOperationType.ADD, "depth" : 6.35 * mm});
        }
        {
            var Q0;
            {var subQ0=sQuery(id+"F29.wireOp",EDGE,"E72");var subQ2=makeQuery(id+"F30.opExtrude","CAP_EDGE",EDGE,{"disambiguationData":[OSD([subQ0])],"isStart":true});Q0=qUnion([makeQuery(id+"F30.boolean.opBoolean","SPLIT",EDGE,{"disambiguationData":[topologyDisambiguationEdgeConnected([makeQuery(id+"F30.opExtrude","CAP_FACE",FACE,{"disambiguationData":[OSD([sQuery(id+"F29.wireOp",EDGE,"E71"),subQ0,sQuery(id+"F29.wireOp",EDGE,"E73"),sQuery(id+"F29.wireOp",EDGE,"E74"),sQuery(id+"F29.wireOp",EDGE,"E80"),sQuery(id+"F29.wireOp",EDGE,"E81"),sQuery(id+"F29.wireOp",EDGE,"E84"),sQuery(id+"F29.wireOp",EDGE,"E85"),sQuery(id+"F29.wireOp",EDGE,"E88.trimOffspring"),sQuery(id+"F29.wireOp",EDGE,"E89"),sQuery(id+"F29.wireOp",EDGE,"E90.MirrorC")])],"isStart":true})])],"derivedFrom":subQ2}),makeQuery(id+"F30.boolean.opBoolean","SPLIT",EDGE,{"disambiguationData":[topologyDisambiguationEdgeConnected([makeQuery(id+"F3.opExtrude","SWEPT_FACE",FACE,{"disambiguationData":[OSD([sQuery(id+"F2.wireOp",EDGE,"E1.right")])]})])],"derivedFrom":subQ2})]);}
            var Q1;
            Q1=makeQuery(id+"F30.opExtrude","CAP_EDGE",EDGE,{"disambiguationData":[OSD([sQuery(id+"F29.wireOp",EDGE,"E84")])],"isStart":true});
            var Q2;
            Q2=makeQuery(id+"F30.opExtrude","CAP_EDGE",EDGE,{"disambiguationData":[OSD([sQuery(id+"F29.wireOp",EDGE,"E80")])],"isStart":true});
            var Q3;
            {var subQ0=sQuery(id+"F29.wireOp",EDGE,"E92");var subQ2=makeQuery(id+"F30.opExtrude","CAP_EDGE",EDGE,{"disambiguationData":[OSD([subQ0])],"isStart":true});Q3=qUnion([makeQuery(id+"F30.boolean.opBoolean","SPLIT",EDGE,{"disambiguationData":[topologyDisambiguationEdgeConnected([makeQuery(id+"F30.opExtrude","CAP_FACE",FACE,{"disambiguationData":[OSD([sQuery(id+"F29.wireOp",EDGE,"E91"),subQ0,sQuery(id+"F29.wireOp",EDGE,"E93"),sQuery(id+"F29.wireOp",EDGE,"E94"),sQuery(id+"F29.wireOp",EDGE,"E100"),sQuery(id+"F29.wireOp",EDGE,"E101"),sQuery(id+"F29.wireOp",EDGE,"E104"),sQuery(id+"F29.wireOp",EDGE,"E105"),sQuery(id+"F29.wireOp",EDGE,"E108.trimOffspring"),sQuery(id+"F29.wireOp",EDGE,"E109"),sQuery(id+"F29.wireOp",EDGE,"E110.MirrorC")])],"isStart":true})])],"derivedFrom":subQ2}),makeQuery(id+"F30.boolean.opBoolean","SPLIT",EDGE,{"disambiguationData":[topologyDisambiguationEdgeConnected([makeQuery(id+"F3.opExtrude","SWEPT_FACE",FACE,{"disambiguationData":[OSD([sQuery(id+"F2.wireOp",EDGE,"E1.right")])]})])],"derivedFrom":subQ2})]);}
            var Q4;
            Q4=makeQuery(id+"F30.opExtrude","CAP_EDGE",EDGE,{"disambiguationData":[OSD([sQuery(id+"F29.wireOp",EDGE,"E100")])],"isStart":true});
            var Q5;
            Q5=makeQuery(id+"F30.opExtrude","CAP_EDGE",EDGE,{"disambiguationData":[OSD([sQuery(id+"F29.wireOp",EDGE,"E104")])],"isStart":true});
            fillet(context, id + "F31", {"entities" : qUnion([Q0, Q1, Q2, Q3, Q4, Q5]), "radius" : 1.27 * mm, "tangentPropagation" : true, "allowEdgeOverflow" : false});
        }
    });
